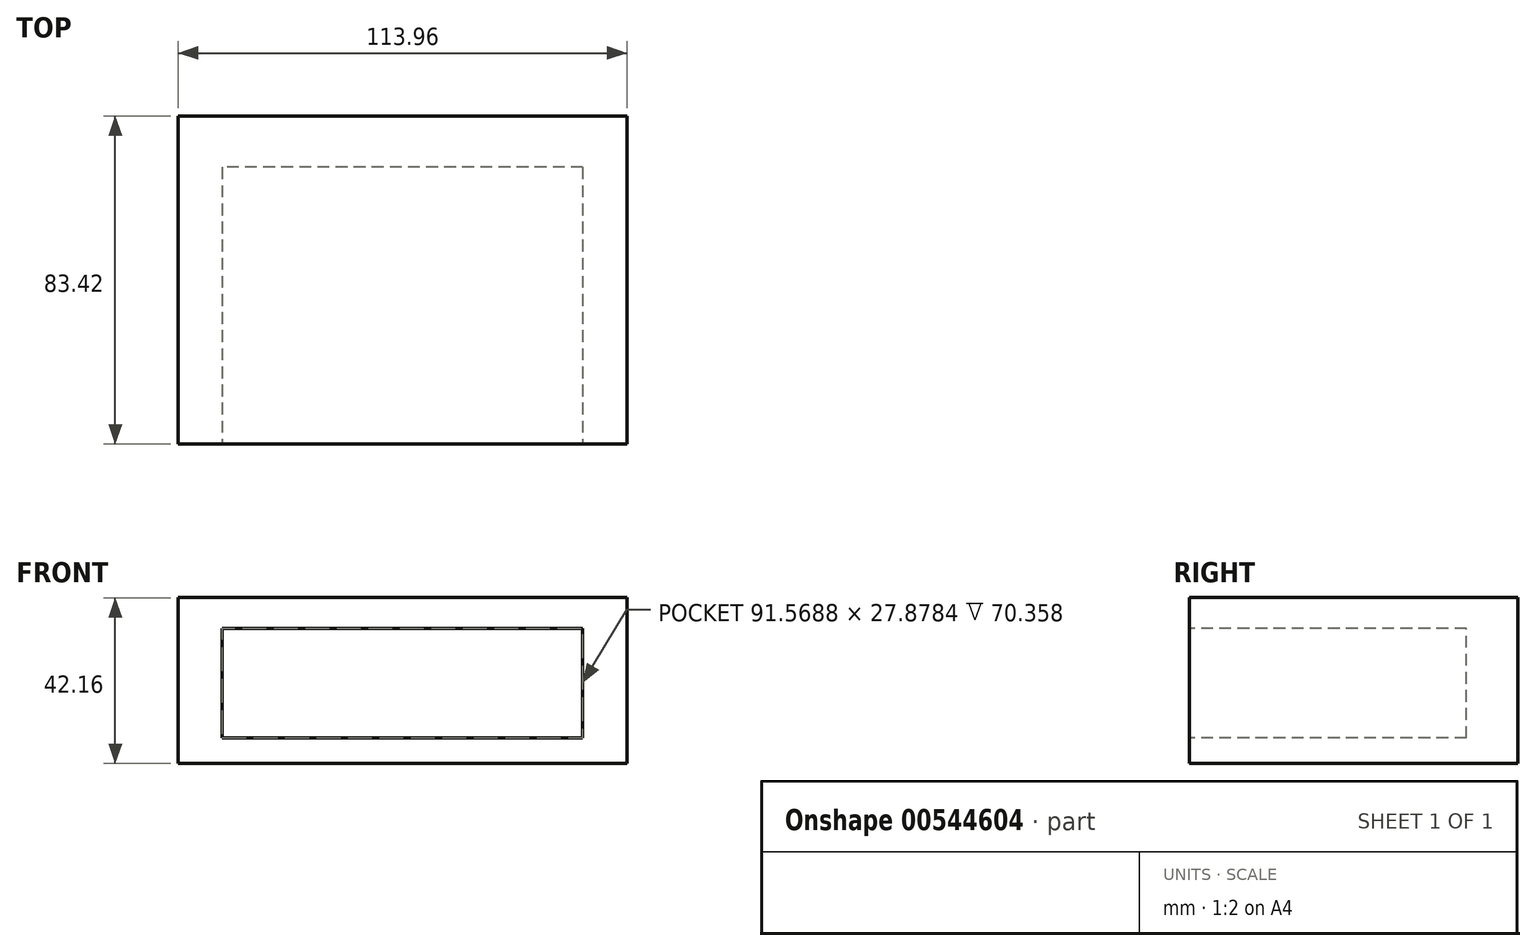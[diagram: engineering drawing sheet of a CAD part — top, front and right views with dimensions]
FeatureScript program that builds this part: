
annotation { "Feature Type Name" : "Feature", "Feature Type Description" : "" }
export const myFeature = defineFeature(function(context is Context, id is Id, definition is map)
    precondition{}
    {
        {
            var Q0;
            Q0=qCreatedBy(makeId("Top.planeOp"),FACE);
            var sketch = newSketch(context, id + "F0", { "sketchPlane" : qUnion([Q0])});
            skLineSegment(sketch, "E0.bottom", {"start": v(56.98, -41.71) * mm, "end": v(-56.98, -41.71) * mm});
            skLineSegment(sketch, "E0.top", {"start": v(56.98, 41.71) * mm, "end": v(-56.98, 41.71) * mm});
            skLineSegment(sketch, "E0.left", {"start": v(56.98, -41.71) * mm, "end": v(56.98, 41.71) * mm});
            skLineSegment(sketch, "E0.right", {"start": v(-56.98, -41.71) * mm, "end": v(-56.98, 41.71) * mm});
            skPoint(sketch, "E0.middle", {"position": v(0, 0) * mm});
            skSolve(sketch);
        }
        {
            var Q0;
            Q0=makeQuery(id+"F0.imprint","IMPRINT",FACE,{"disambiguationData":[TD([[makeQuery(id+"F0.imprint","IMPRINT",EDGE,{"derivedFrom":sQuery(id+"F0.wireOp",EDGE,"E0.bottom")}),-1.0]])]});
            extrude(context, id + "F1", {"entities" : qUnion([Q0]), "depth" : 42.16 * mm, "offsetDistance" : 25.4 * mm});
        }
        {
            var Q0;
            Q0=makeQuery(id+"F1.opExtrude","SWEPT_FACE",FACE,{"disambiguationData":[OSD([sQuery(id+"F0.wireOp",EDGE,"E0.bottom")])]});
            var sketch = newSketch(context, id + "F2", { "sketchPlane" : qUnion([Q0])});
            skLineSegment(sketch, "E1.bottom", {"start": v(45.78, 6.5) * mm, "end": v(-45.78, 6.5) * mm});
            skLineSegment(sketch, "E1.top", {"start": v(45.78, 34.39) * mm, "end": v(-45.78, 34.39) * mm});
            skLineSegment(sketch, "E1.left", {"start": v(45.78, 6.5) * mm, "end": v(45.78, 34.39) * mm});
            skLineSegment(sketch, "E1.right", {"start": v(-45.78, 6.5) * mm, "end": v(-45.78, 34.39) * mm});
            skPoint(sketch, "E1.middle", {"position": v(0, 20.45) * mm});
            skSolve(sketch);
        }
        {
            var Q0;
            Q0 = qSketchRegion(id + "F2", true);
            extrude(context, id + "F3", {"entities" : qUnion([Q0]), "operationType" : NewBodyOperationType.REMOVE, "oppositeDirection" : true, "depth" : 70.36 * mm, "offsetDistance" : 25.4 * mm});
        }
    });
